# Revit family: QF_ELECTROLUXPROFESSIONAL_391574_E9AAMTBCMEI
name_source: partatom
category: Attrezzature speciali
revit_build: Autodesk Revit 2018 (Build: 20181011_1500(x64)
units: mm (PartAtom-declared; Revit-internal decimal feet)

## family parameters
Basato su piano di lavoro = No
Condiviso = No
Punto di calcolo locali = No
Quota connettore circolare = Usa diametro
Sempre verticale = Sì
Taglio con vuoti quando caricato = No
Tipo di parte = Normale

## types (1)
- Standard
    Accessory = Sì
    Cold Water Size = 0"
    Compressed Air Pressure = 0.00 psi
    Compressed Air Size = 0"
    Compressed Air Volume = 0 GPM
    Condensate Return Size = 0"
    Cycle = 50 Hz
    Depth Actual = 930 mm  [stored 3.05118 ft]
    Descrizione = 4-BURNER GAS RANGE+ELECTRIC OVEN 800MM - QMARK
    Direct Waste Size = 0"
    Gas Input Pressure = 0.7
    Gas KW = 28
    Gas Size = 1"
    HP = 8 HP
    Height Actual = 850 mm  [stored 2.78871 ft]
    Hot Water Size = 0"
    Item Number = 391574
    Length Actual = 800 mm  [stored 2.62467 ft]
    Modello = E9AAMTBCMEI
    Phase = 3
    Produttore = Electrolux Professional
    Refrigerant Compressor Remote = Sì
    Refrigeration Liquid Line Size = 0 mm  [stored 0 ft]
    Refrigeration Suction Line Size = 0 mm  [stored 0 ft]
    Steam Consumption per Hour = 0
    Steam Supply Maximum Pressure = 0.00 psi
    Steam Supply Minimum Pressure = 0.00 psi
    Steam Supply Size = 0"
    URL = https://www.electroluxprofessional.com
    URL Manufacturer = https://www.electroluxprofessional.com
    Volts = 380 V
    Watts = 6000 W
    Weight = 155.00 kg

note: source unit labels omitted for Gas Input Pressure — the stored unit's dimension contradicts the parameter name (converter mislabeling)

note: [stored X ft] marks values corroborated as IEEE doubles in the binary element streams (Revit-internal decimal feet)

## geometry (parser evidence)
native form markers: Blend x20, Sweep x5
no freeform markers — native parametric forms only
